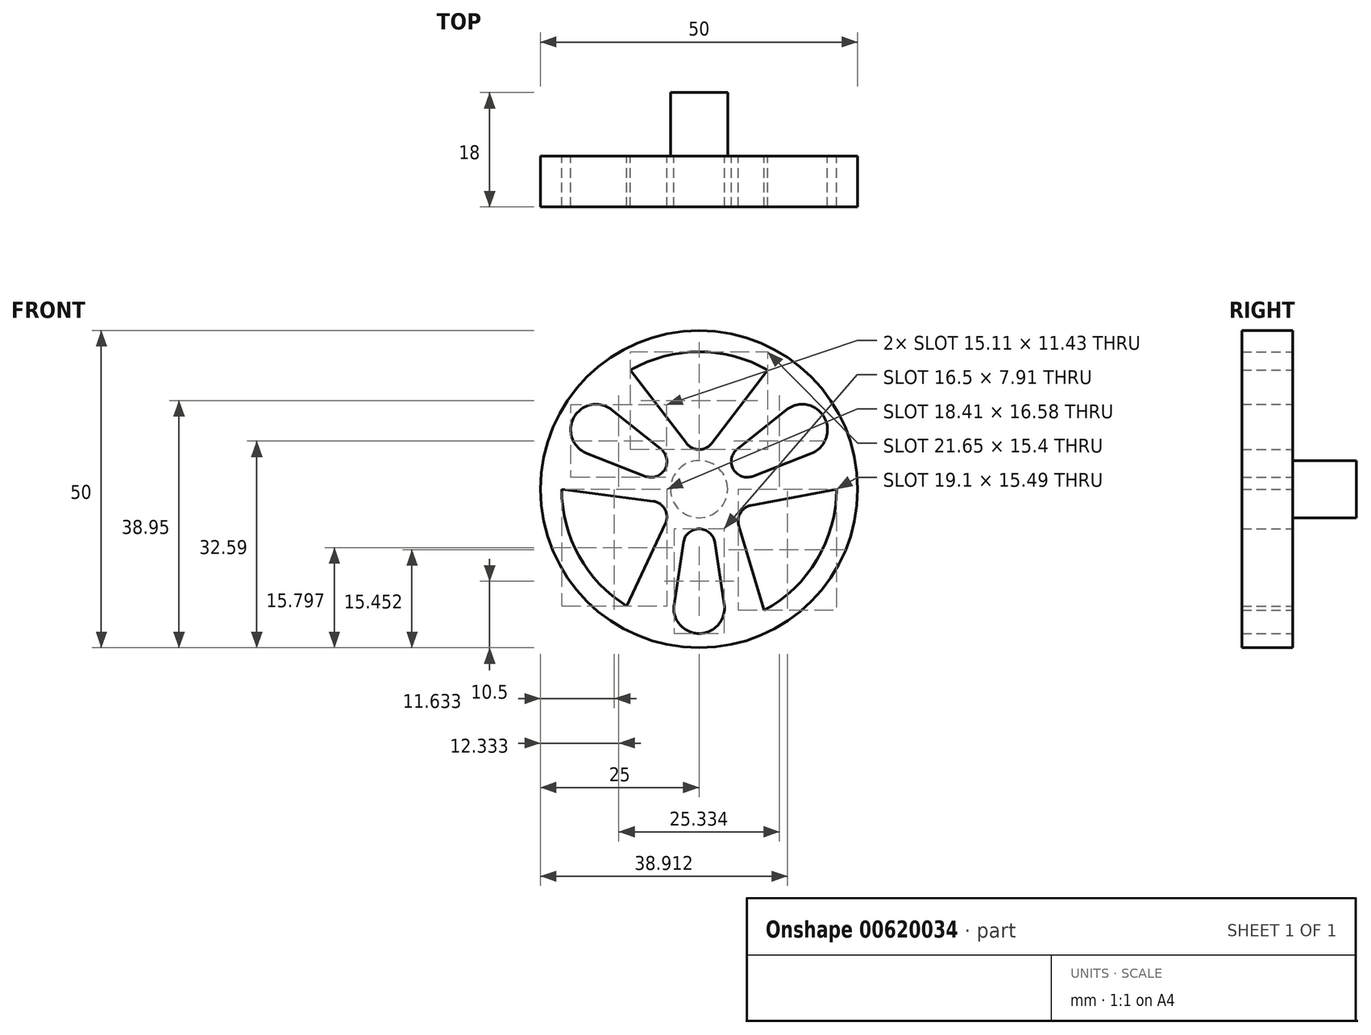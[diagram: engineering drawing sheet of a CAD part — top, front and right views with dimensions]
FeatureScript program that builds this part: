
annotation { "Feature Type Name" : "Feature", "Feature Type Description" : "" }
export const myFeature = defineFeature(function(context is Context, id is Id, definition is map)
    precondition{}
    {
        {
            var Q0;
            Q0=qCreatedBy(makeId("Front.planeOp"),FACE);
            var sketch = newSketch(context, id + "F0", { "sketchPlane" : qUnion([Q0])});
            skCircle(sketch, "E0", {"center": v(0, 0) * mm, "radius": 25 * mm});
            skCircle(sketch, "E1", {"center": v(0, 0) * mm, "radius": 12.5 * mm, "construction": true});
            skCircle(sketch, "E2.cCircle", {"center": v(0, 0) * mm, "radius": 25 * mm, "construction": true});
            skLineSegment(sketch, "E2.0", {"start": v(0, 25) * mm, "end": v(21.65, 12.5) * mm, "construction": true});
            skLineSegment(sketch, "E2.1", {"start": v(21.65, 12.5) * mm, "end": v(21.65, -12.5) * mm, "construction": true});
            skLineSegment(sketch, "E2.2", {"start": v(21.65, -12.5) * mm, "end": v(0, -25) * mm, "construction": true});
            skLineSegment(sketch, "E2.3", {"start": v(0, -25) * mm, "end": v(-21.65, -12.5) * mm, "construction": true});
            skLineSegment(sketch, "E2.4", {"start": v(-21.65, -12.5) * mm, "end": v(-21.65, 12.5) * mm, "construction": true});
            skLineSegment(sketch, "E2.5", {"start": v(-21.65, 12.5) * mm, "end": v(0, 25) * mm, "construction": true});
            skLineSegment(sketch, "E3", {"start": v(-21.65, 12.5) * mm, "end": v(0, 0) * mm, "construction": true});
            skLineSegment(sketch, "E4", {"start": v(0, 25) * mm, "end": v(0, 0) * mm, "construction": true});
            skLineSegment(sketch, "E5", {"start": v(0, 0) * mm, "end": v(-21.65, -12.5) * mm, "construction": true});
            skLineSegment(sketch, "E6", {"start": v(0, -25) * mm, "end": v(0, 0) * mm, "construction": true});
            skLineSegment(sketch, "E7", {"start": v(0, 0) * mm, "end": v(25, 0) * mm, "construction": true});
            skLineSegment(sketch, "E8", {"start": v(21.65, 12.5) * mm, "end": v(0, 0) * mm, "construction": true});
            skLineSegment(sketch, "E9", {"start": v(0, 0) * mm, "end": v(21.65, -12.5) * mm, "construction": true});
            skCircle(sketch, "E10", {"center": v(0, 0) * mm, "radius": 18.75 * mm, "construction": true});
            skLineSegment(sketch, "E11.0", {"start": v(18.75, 0) * mm, "end": v(9.38, -16.24) * mm, "construction": true});
            skLineSegment(sketch, "E11.1", {"start": v(9.38, -16.24) * mm, "end": v(-9.37, -16.24) * mm, "construction": true});
            skLineSegment(sketch, "E11.2", {"start": v(-9.37, -16.24) * mm, "end": v(-18.75, 0) * mm, "construction": true});
            skLineSegment(sketch, "E11.3", {"start": v(-18.75, 0) * mm, "end": v(-9.38, 16.24) * mm, "construction": true});
            skLineSegment(sketch, "E11.4", {"start": v(-9.38, 16.24) * mm, "end": v(9.37, 16.24) * mm, "construction": true});
            skLineSegment(sketch, "E11.5", {"start": v(9.37, 16.24) * mm, "end": v(18.75, 0) * mm, "construction": true});
            skCircle(sketch, "E12", {"center": v(0, 0) * mm, "radius": 7.5 * mm, "construction": true});
            skLineSegment(sketch, "E13", {"start": v(-21.65, 12.5) * mm, "end": v(-10.83, 18.75) * mm, "construction": true});
            skLineSegment(sketch, "E14", {"start": v(-10.83, 18.75) * mm, "end": v(-1.44, 6.52) * mm});
            skLineSegment(sketch, "E15", {"start": v(10.83, 18.75) * mm, "end": v(1.44, 6.52) * mm});
            skArc(sketch, "E16", {"start": v(10.83, 18.75) * mm, "mid": v(0, 21.65) * mm, "end": v(-10.83, 18.75) * mm});
            skLineSegment(sketch, "E17", {"start": v(-21.66, 0) * mm, "end": v(-6.37, -2.01) * mm});
            skLineSegment(sketch, "E18", {"start": v(-11.42, -18.4) * mm, "end": v(-4.92, -4.6) * mm});
            skArc(sketch, "E19.trimOffspring", {"start": v(10.23, -19.1) * mm, "mid": v(18.7, -10.92) * mm, "end": v(21.65, 0.48) * mm});
            skArc(sketch, "E20.trimOffspring", {"start": v(-21.65, 0.48) * mm, "mid": v(-18.7, -10.92) * mm, "end": v(-10.23, -19.1) * mm});
            skLineSegment(sketch, "E21", {"start": v(10.23, -19.1) * mm, "end": v(5.93, -4.59) * mm});
            skLineSegment(sketch, "E22", {"start": v(21.66, 0) * mm, "end": v(6.97, -2.78) * mm});
            skCircle(sketch, "E23", {"center": v(-16.24, 9.37) * mm, "radius": 4 * mm});
            skLineSegment(sketch, "E24", {"start": v(-4.48, 0.48) * mm, "end": v(-22.33, 7.46) * mm});
            skLineSegment(sketch, "E25", {"start": v(-16.1, 14.4) * mm, "end": v(-3.09, 3.99) * mm});
            skCircle(sketch, "E26", {"center": v(16.24, 9.38) * mm, "radius": 4 * mm});
            skCircle(sketch, "E27", {"center": v(0, -18.75) * mm, "radius": 4 * mm});
            skLineSegment(sketch, "E28", {"start": v(-4.43, -21.3) * mm, "end": v(-1.92, -4.75) * mm});
            skLineSegment(sketch, "E29", {"start": v(4.42, -21.2) * mm, "end": v(1.95, -4.96) * mm});
            skLineSegment(sketch, "E30", {"start": v(20.6, 6.79) * mm, "end": v(5.55, 0.9) * mm});
            skLineSegment(sketch, "E31", {"start": v(3.1, 3.99) * mm, "end": v(15.37, 13.8) * mm});
            skCircle(sketch, "E32", {"center": v(0, 0) * mm, "radius": 27 * mm});
            skCircle(sketch, "E33", {"center": v(0, 0) * mm, "radius": 10 * mm, "construction": true});
            skCircle(sketch, "E34", {"center": v(8.66, -5) * mm, "radius": 2.5 * mm});
            skCircle(sketch, "E35", {"center": v(0, 0) * mm, "radius": 8.75 * mm, "construction": true});
            skCircle(sketch, "E36", {"center": v(7.58, 4.38) * mm, "radius": 2.5 * mm});
            skCircle(sketch, "E37", {"center": v(0, 8.75) * mm, "radius": 2.5 * mm});
            skCircle(sketch, "E38", {"center": v(-7.58, 4.37) * mm, "radius": 2.5 * mm});
            skCircle(sketch, "E39", {"center": v(-7.58, -4.38) * mm, "radius": 2.5 * mm});
            skCircle(sketch, "E40", {"center": v(0, -8.75) * mm, "radius": 2.5 * mm});
            skSolve(sketch);
        }
        {
            var Q0;
            Q0=makeQuery(id+"F0.imprint","IMPRINT",FACE,{"disambiguationData":[TD([[makeQuery(id+"F0.imprint","IMPRINT",EDGE,{"derivedFrom":sQuery(id+"F0.wireOp",EDGE,"E0")}),1.0]])]});
            extrude(context, id + "F1", {"entities" : qUnion([Q0]), "depth" : 8 * mm, "offsetDistance" : 25 * mm});
        }
        {
            var Q0;
            Q0=makeQuery(id+"F1.opExtrude","CAP_FACE",FACE,{"disambiguationData":[OSD([sQuery(id+"F0.wireOp",EDGE,"E0"),sQuery(id+"F0.wireOp",EDGE,"snchJbhh-FD0Y-bEI3-yXhw-i09hzjSmrZee"),sQuery(id+"F0.wireOp",EDGE,"fO32A7Xi-dkgM-ytpq-YN5s-FzLaEzQa29w4"),sQuery(id+"F0.wireOp",EDGE,"9ERNPApv-8uSE-PtJ5-ctgE-cKity0kQLgRk"),sQuery(id+"F0.wireOp",EDGE,"13cFJKZy-oMBF-au1c-HTQc-IjUGtHiG7lko"),sQuery(id+"F0.wireOp",EDGE,"N3Sdt1DQ-IZq0-0At5-yWDq-YoBXizgjMUti"),sQuery(id+"F0.wireOp",EDGE,"MwEtPBmZ-dWJm-hYmZ-Jmu3-C0zlyG3PIoy8"),sQuery(id+"F0.wireOp",EDGE,"E14"),sQuery(id+"F0.wireOp",EDGE,"E15"),sQuery(id+"F0.wireOp",EDGE,"E16"),sQuery(id+"F0.wireOp",EDGE,"E17"),sQuery(id+"F0.wireOp",EDGE,"E18"),sQuery(id+"F0.wireOp",EDGE,"E19.trimOffspring"),sQuery(id+"F0.wireOp",EDGE,"E20.trimOffspring"),sQuery(id+"F0.wireOp",EDGE,"E21"),sQuery(id+"F0.wireOp",EDGE,"E22"),sQuery(id+"F0.wireOp",EDGE,"E23"),sQuery(id+"F0.wireOp",EDGE,"E24"),sQuery(id+"F0.wireOp",EDGE,"E25"),sQuery(id+"F0.wireOp",EDGE,"E26"),sQuery(id+"F0.wireOp",EDGE,"E27"),sQuery(id+"F0.wireOp",EDGE,"E28"),sQuery(id+"F0.wireOp",EDGE,"E29"),sQuery(id+"F0.wireOp",EDGE,"E30"),sQuery(id+"F0.wireOp",EDGE,"E31")])],"isStart":true});
            var sketch = newSketch(context, id + "F2", { "sketchPlane" : qUnion([Q0])});
            skCircle(sketch, "E41", {"center": v(0, 0) * mm, "radius": 4.5 * mm});
            skSolve(sketch);
        }
        {
            var Q0;
            Q0=makeQuery(id+"F2.imprint","IMPRINT",FACE,{"disambiguationData":[TD([[makeQuery(id+"F2.imprint","IMPRINT",EDGE,{"derivedFrom":sQuery(id+"F2.wireOp",EDGE,"E41")}),1.0]])]});
            extrude(context, id + "F3", {"entities" : qUnion([Q0]), "operationType" : NewBodyOperationType.ADD, "depth" : 10 * mm, "offsetDistance" : 25 * mm});
        }
    });
